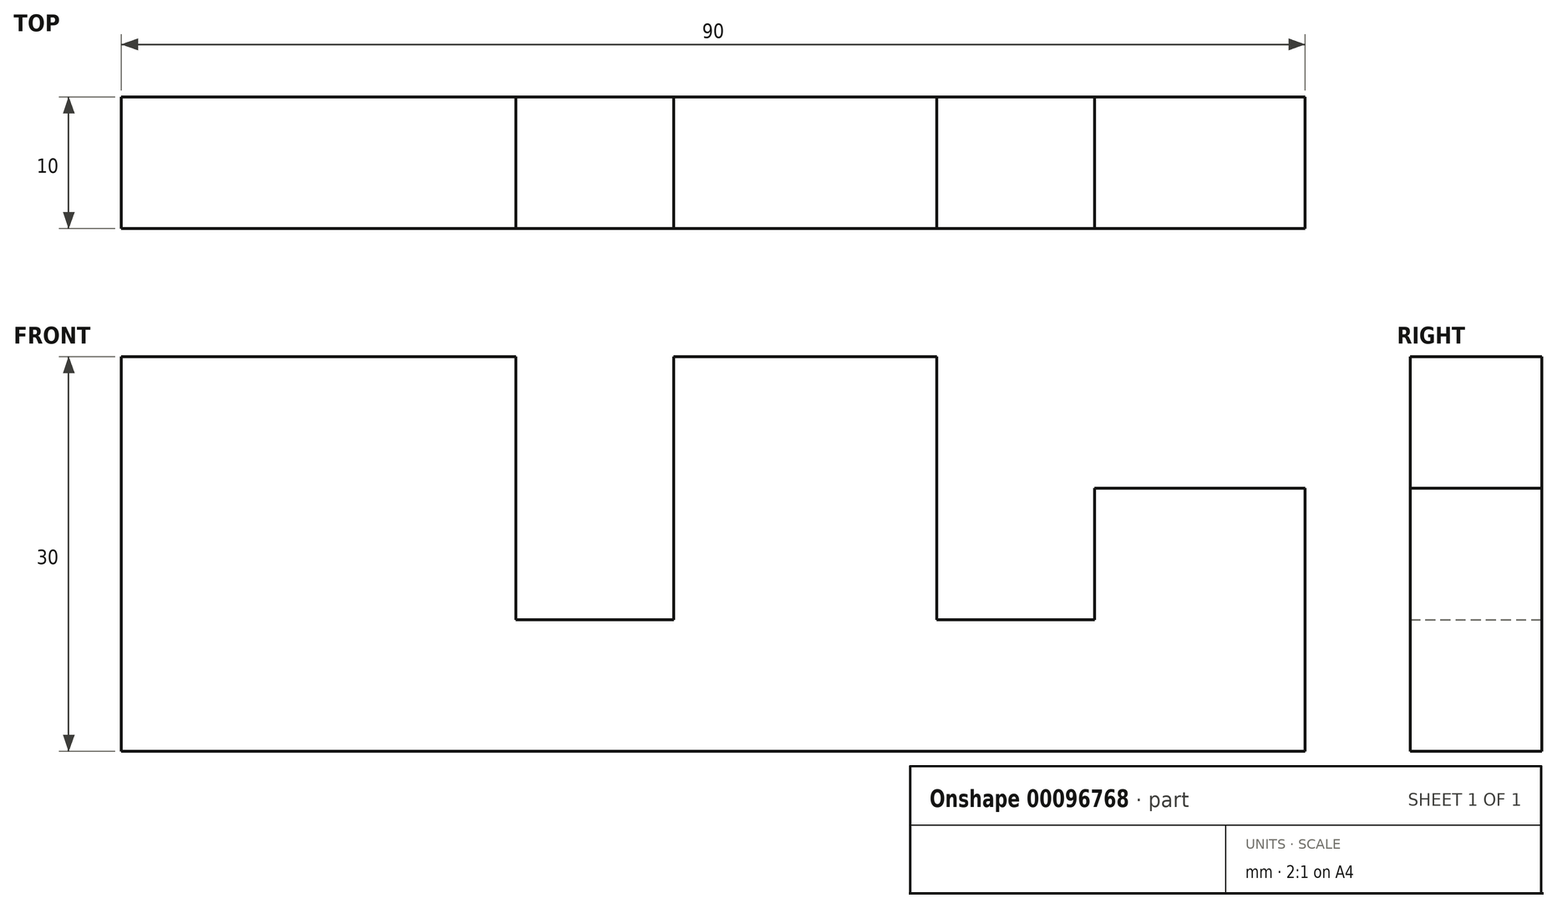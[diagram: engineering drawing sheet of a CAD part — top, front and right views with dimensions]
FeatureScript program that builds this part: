
annotation { "Feature Type Name" : "Feature", "Feature Type Description" : "" }
export const myFeature = defineFeature(function(context is Context, id is Id, definition is map)
    precondition{}
    {
        {
            var Q0;
            Q0=qCreatedBy(makeId("Front.planeOp"),FACE);
            var sketch = newSketch(context, id + "F0", { "sketchPlane" : qUnion([Q0])});
            skLineSegment(sketch, "E0", {"start": v(0, 0) * mm, "end": v(0, 30) * mm});
            skLineSegment(sketch, "E1", {"start": v(0, 30) * mm, "end": v(30, 30) * mm});
            skLineSegment(sketch, "E2", {"start": v(30, 30) * mm, "end": v(30, 10) * mm});
            skLineSegment(sketch, "E3", {"start": v(30, 10) * mm, "end": v(42, 10) * mm});
            skLineSegment(sketch, "E4", {"start": v(42, 10) * mm, "end": v(42, 30) * mm});
            skLineSegment(sketch, "E5", {"start": v(42, 30) * mm, "end": v(62, 30) * mm});
            skLineSegment(sketch, "E6", {"start": v(62, 30) * mm, "end": v(62, 10) * mm});
            skLineSegment(sketch, "E7", {"start": v(62, 10) * mm, "end": v(74, 10) * mm});
            skLineSegment(sketch, "E8", {"start": v(74, 10) * mm, "end": v(74, 20) * mm});
            skLineSegment(sketch, "E9", {"start": v(74, 20) * mm, "end": v(90, 20) * mm});
            skLineSegment(sketch, "E10", {"start": v(90, 20) * mm, "end": v(90, 0) * mm});
            skLineSegment(sketch, "E11", {"start": v(90, 0) * mm, "end": v(0, 0) * mm});
            skSolve(sketch);
        }
        {
            var Q0;
            Q0 = qSketchRegion(id + "F0", true);
            extrude(context, id + "F1", {"entities" : qUnion([Q0]), "depth" : 10 * mm});
        }
    });
